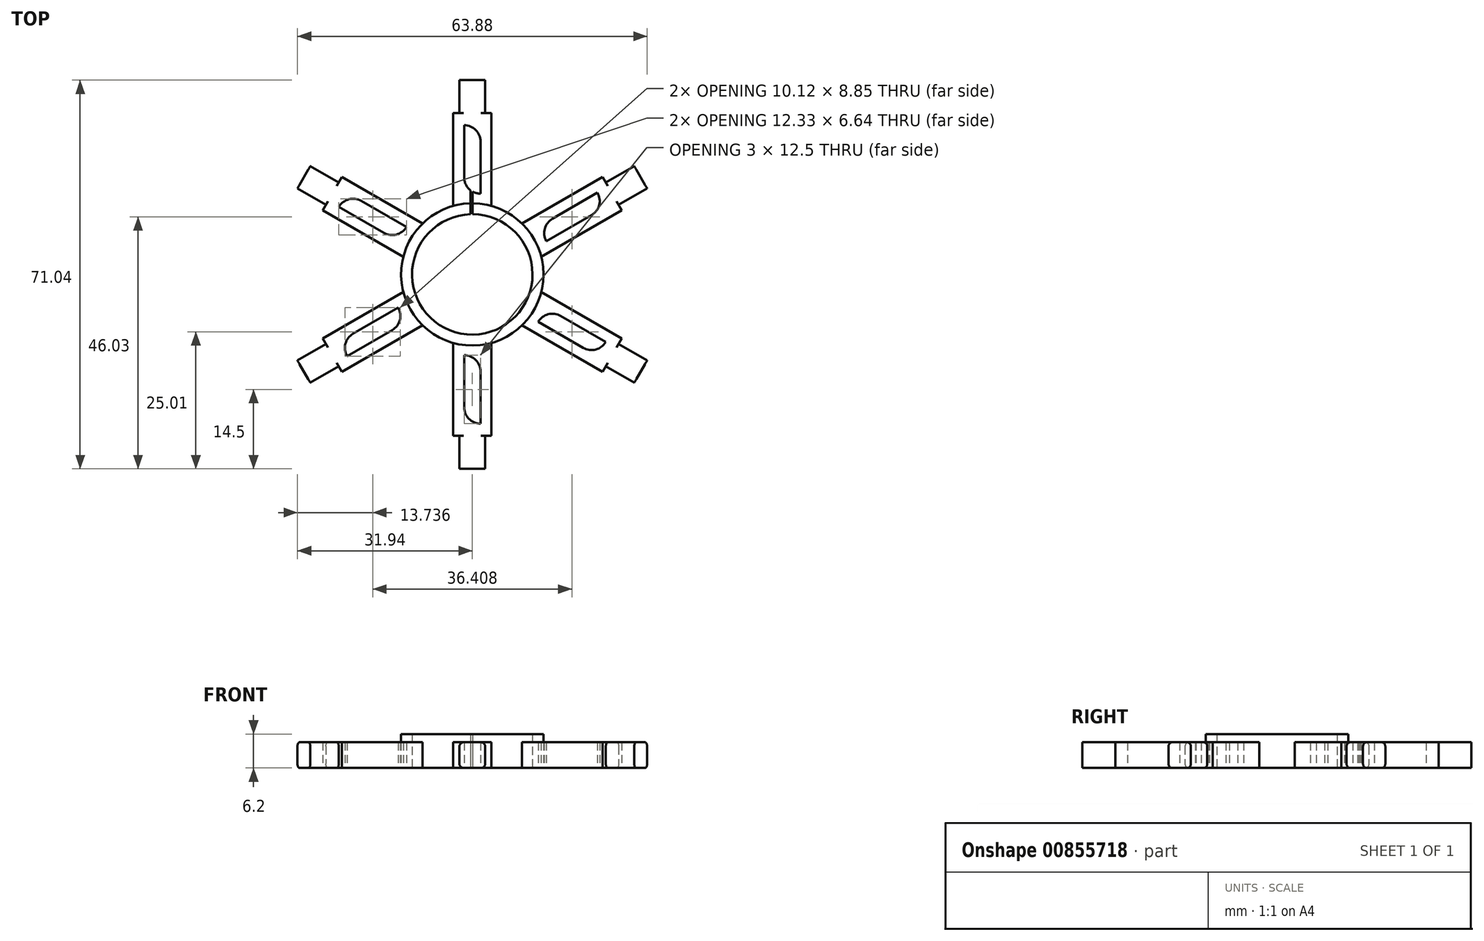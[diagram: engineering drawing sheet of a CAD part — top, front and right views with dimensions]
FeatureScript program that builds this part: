
annotation { "Feature Type Name" : "Feature", "Feature Type Description" : "" }
export const myFeature = defineFeature(function(context is Context, id is Id, definition is map)
    precondition{}
    {
        {
            var Q0;
            Q0=qCreatedBy(makeId("Top.planeOp"),FACE);
            var sketch = newSketch(context, id + "F0", { "sketchPlane" : qUnion([Q0])});
            skCircle(sketch, "E0", {"center": v(0, 0) * mm, "radius": 11 * mm});
            skCircle(sketch, "E1", {"center": v(0, 0) * mm, "radius": 13 * mm});
            skLineSegment(sketch, "E2.top", {"start": v(3.5, 29.52) * mm, "end": v(-3.5, 29.52) * mm});
            skLineSegment(sketch, "E2.left", {"start": v(3.5, 12.52) * mm, "end": v(3.5, 29.52) * mm});
            skLineSegment(sketch, "E2.right", {"start": v(-3.5, 12.52) * mm, "end": v(-3.5, 29.52) * mm});
            skPoint(sketch, "E2.middle", {"position": v(0, 21.02) * mm});
            skLineSegment(sketch, "E3.bottom", {"start": v(2.35, 29.52) * mm, "end": v(-2.35, 29.52) * mm});
            skLineSegment(sketch, "E3.top", {"start": v(2.35, 35.52) * mm, "end": v(-2.35, 35.52) * mm});
            skLineSegment(sketch, "E3.left", {"start": v(2.35, 29.52) * mm, "end": v(2.35, 35.52) * mm});
            skLineSegment(sketch, "E3.right", {"start": v(-2.35, 29.52) * mm, "end": v(-2.35, 35.52) * mm});
            skPoint(sketch, "E3.middle", {"position": v(0, 32.52) * mm});
            skLineSegment(sketch, "E4.bottom", {"start": v(1.5, 14.77) * mm, "end": v(1.5, 14.77) * mm});
            skLineSegment(sketch, "E4.top", {"start": v(-1.5, 27.27) * mm, "end": v(-1.5, 27.27) * mm});
            skLineSegment(sketch, "E4.left", {"start": v(1.5, 14.77) * mm, "end": v(1.5, 24.27) * mm});
            skLineSegment(sketch, "E4.right", {"start": v(-1.5, 17.77) * mm, "end": v(-1.5, 27.27) * mm});
            skPoint(sketch, "E5.visualSharp", {"position": v(-1.5, 14.77) * mm});
            skArc(sketch, "E5.filletArc", {"start": v(-1.5, 17.77) * mm, "mid": v(-0.62, 15.65) * mm, "end": v(1.5, 14.77) * mm});
            skPoint(sketch, "E6.visualSharp", {"position": v(1.5, 27.27) * mm});
            skArc(sketch, "E6.filletArc", {"start": v(1.5, 24.27) * mm, "mid": v(0.62, 26.4) * mm, "end": v(-1.5, 27.27) * mm});
            skSolve(sketch);
        }
        {
            var Q0;
            Q0=qCreatedBy(makeId("Top.planeOp"),FACE);
            var sketch = newSketch(context, id + "F1", { "sketchPlane" : qUnion([Q0])});
            skLineSegment(sketch, "E7.bottom", {"start": v(0.05, 15.5) * mm, "end": v(-0.3, 15.5) * mm});
            skLineSegment(sketch, "E7.top", {"start": v(0.05, 10.56) * mm, "end": v(-0.3, 10.56) * mm});
            skLineSegment(sketch, "E7.left", {"start": v(0.05, 15.5) * mm, "end": v(0.05, 10.56) * mm});
            skLineSegment(sketch, "E7.right", {"start": v(-0.3, 15.5) * mm, "end": v(-0.3, 10.56) * mm});
            skSolve(sketch);
        }
        {
            var Q0;
            Q0=makeQuery(id+"F0.imprint","IMPRINT",FACE,{"disambiguationData":[TD([[makeQuery(id+"F0.imprint","IMPRINT",EDGE,{"derivedFrom":sQuery(id+"F0.wireOp",EDGE,"E0")}),-1.0]])]});
            extrude(context, id + "F2", {"entities" : qUnion([Q0]), "depth" : 6.2 * mm, "offsetDistance" : 25.4 * mm});
        }
        {
            var Q0;
            {var subQ1=sQuery(id+"F0.wireOp",EDGE,"E2.left");Q0=makeQuery(id+"F0.imprint","IMPRINT",FACE,{"disambiguationData":[TD([[makeQuery(id+"F0.imprint","IMPRINT",EDGE,{"derivedFrom":subQ1}),1.0]])]});}
            var Q1;
            Q1=makeQuery(id+"F0.imprint","IMPRINT",FACE,{"disambiguationData":[TD([[makeQuery(id+"F0.imprint","IMPRINT",EDGE,{"derivedFrom":sQuery(id+"F0.wireOp",EDGE,"E3.top")}),1.0]])]});
            extrude(context, id + "F3", {"entities" : qUnion([Q0, Q1]), "operationType" : NewBodyOperationType.ADD, "depth" : 4.7 * mm, "offsetDistance" : 25.4 * mm});
        }
        {
            var Q0;
            Q0=makeQuery(id+"F2.opExtrude","SWEPT_BODY",BODY,{"disambiguationData":[OSD([sQuery(id+"F0.wireOp",EDGE,"E0"),sQuery(id+"F0.wireOp",EDGE,"E1")])]});
            var Q1;
            Q1=sQuery(id+"F0.wireOp",EDGE,"E0");
            circularPattern(context, id + "F4", {"operationType" : NewBodyOperationType.ADD, "entities" : qUnion([Q0]), "axis" : qUnion([Q1]), "angle" : 360 * degree, "instanceCount" : 6, "equalSpace" : true});
        }
        {
            var Q0;
            Q0 = qSketchRegion(id + "F1", true);
            extrude(context, id + "F5", {"entities" : qUnion([Q0]), "operationType" : NewBodyOperationType.REMOVE, "depth" : 25.4 * mm, "offsetDistance" : 25.4 * mm});
        }
        {
            var Q0;
            Q0=makeQuery(id+"F4.opPattern","COPY",EDGE,{"derivedFrom":makeQuery(id+"F3.opExtrude","CAP_EDGE",EDGE,{"disambiguationData":[OSD([sQuery(id+"F0.wireOp",EDGE,"E3.right")])],"isStart":false}),"instanceName":"2"});
            var Q1;
            Q1=makeQuery(id+"F4.opPattern","COPY",EDGE,{"derivedFrom":makeQuery(id+"F3.opExtrude","CAP_EDGE",EDGE,{"disambiguationData":[OSD([sQuery(id+"F0.wireOp",EDGE,"E3.left")])],"isStart":false}),"instanceName":"2"});
            var Q2;
            Q2=makeQuery(id+"F4.opPattern","COPY",EDGE,{"derivedFrom":makeQuery(id+"F3.opExtrude","CAP_EDGE",EDGE,{"disambiguationData":[OSD([sQuery(id+"F0.wireOp",EDGE,"E3.right")])],"isStart":true}),"instanceName":"2"});
            var Q3;
            Q3=makeQuery(id+"F4.opPattern","COPY",EDGE,{"derivedFrom":makeQuery(id+"F3.opExtrude","CAP_EDGE",EDGE,{"disambiguationData":[OSD([sQuery(id+"F0.wireOp",EDGE,"E3.left")])],"isStart":true}),"instanceName":"2"});
            var Q4;
            Q4=makeQuery(id+"F4.opPattern","COPY",EDGE,{"derivedFrom":makeQuery(id+"F3.opExtrude","CAP_EDGE",EDGE,{"disambiguationData":[OSD([sQuery(id+"F0.wireOp",EDGE,"E3.left")])],"isStart":true}),"instanceName":"3"});
            var Q5;
            Q5=makeQuery(id+"F4.opPattern","COPY",EDGE,{"derivedFrom":makeQuery(id+"F3.opExtrude","CAP_EDGE",EDGE,{"disambiguationData":[OSD([sQuery(id+"F0.wireOp",EDGE,"E3.left")])],"isStart":false}),"instanceName":"3"});
            var Q6;
            Q6=makeQuery(id+"F4.opPattern","COPY",EDGE,{"derivedFrom":makeQuery(id+"F3.opExtrude","CAP_EDGE",EDGE,{"disambiguationData":[OSD([sQuery(id+"F0.wireOp",EDGE,"E3.right")])],"isStart":false}),"instanceName":"3"});
            var Q7;
            Q7=makeQuery(id+"F4.opPattern","COPY",EDGE,{"derivedFrom":makeQuery(id+"F3.opExtrude","CAP_EDGE",EDGE,{"disambiguationData":[OSD([sQuery(id+"F0.wireOp",EDGE,"E3.right")])],"isStart":true}),"instanceName":"3"});
            var Q8;
            Q8=makeQuery(id+"F4.opPattern","COPY",EDGE,{"derivedFrom":makeQuery(id+"F3.opExtrude","CAP_EDGE",EDGE,{"disambiguationData":[OSD([sQuery(id+"F0.wireOp",EDGE,"E3.left")])],"isStart":false}),"instanceName":"4"});
            var Q9;
            Q9=makeQuery(id+"F4.opPattern","COPY",EDGE,{"derivedFrom":makeQuery(id+"F3.opExtrude","CAP_EDGE",EDGE,{"disambiguationData":[OSD([sQuery(id+"F0.wireOp",EDGE,"E3.left")])],"isStart":true}),"instanceName":"4"});
            var Q10;
            Q10=makeQuery(id+"F4.opPattern","COPY",EDGE,{"derivedFrom":makeQuery(id+"F3.opExtrude","CAP_EDGE",EDGE,{"disambiguationData":[OSD([sQuery(id+"F0.wireOp",EDGE,"E3.right")])],"isStart":false}),"instanceName":"4"});
            var Q11;
            Q11=makeQuery(id+"F4.opPattern","COPY",EDGE,{"derivedFrom":makeQuery(id+"F3.opExtrude","CAP_EDGE",EDGE,{"disambiguationData":[OSD([sQuery(id+"F0.wireOp",EDGE,"E3.right")])],"isStart":true}),"instanceName":"4"});
            var Q12;
            Q12=makeQuery(id+"F4.opPattern","COPY",EDGE,{"derivedFrom":makeQuery(id+"F3.opExtrude","CAP_EDGE",EDGE,{"disambiguationData":[OSD([sQuery(id+"F0.wireOp",EDGE,"E3.left")])],"isStart":false}),"instanceName":"5"});
            var Q13;
            Q13=makeQuery(id+"F4.opPattern","COPY",EDGE,{"derivedFrom":makeQuery(id+"F3.opExtrude","CAP_EDGE",EDGE,{"disambiguationData":[OSD([sQuery(id+"F0.wireOp",EDGE,"E3.left")])],"isStart":true}),"instanceName":"5"});
            var Q14;
            Q14=makeQuery(id+"F4.opPattern","COPY",EDGE,{"derivedFrom":makeQuery(id+"F3.opExtrude","CAP_EDGE",EDGE,{"disambiguationData":[OSD([sQuery(id+"F0.wireOp",EDGE,"E3.right")])],"isStart":false}),"instanceName":"5"});
            var Q15;
            Q15=makeQuery(id+"F4.opPattern","COPY",EDGE,{"derivedFrom":makeQuery(id+"F3.opExtrude","CAP_EDGE",EDGE,{"disambiguationData":[OSD([sQuery(id+"F0.wireOp",EDGE,"E3.right")])],"isStart":true}),"instanceName":"5"});
            var Q16;
            Q16=makeQuery(id+"F3.opExtrude","CAP_EDGE",EDGE,{"disambiguationData":[OSD([sQuery(id+"F0.wireOp",EDGE,"E3.left")])],"isStart":false});
            var Q17;
            Q17=makeQuery(id+"F3.opExtrude","CAP_EDGE",EDGE,{"disambiguationData":[OSD([sQuery(id+"F0.wireOp",EDGE,"E3.left")])],"isStart":true});
            var Q18;
            Q18=makeQuery(id+"F3.opExtrude","CAP_EDGE",EDGE,{"disambiguationData":[OSD([sQuery(id+"F0.wireOp",EDGE,"E3.right")])],"isStart":false});
            var Q19;
            Q19=makeQuery(id+"F3.opExtrude","CAP_EDGE",EDGE,{"disambiguationData":[OSD([sQuery(id+"F0.wireOp",EDGE,"E3.right")])],"isStart":true});
            var Q20;
            Q20=makeQuery(id+"F4.opPattern","COPY",EDGE,{"derivedFrom":makeQuery(id+"F3.opExtrude","CAP_EDGE",EDGE,{"disambiguationData":[OSD([sQuery(id+"F0.wireOp",EDGE,"E3.left")])],"isStart":false}),"instanceName":"1"});
            var Q21;
            Q21=makeQuery(id+"F4.opPattern","COPY",EDGE,{"derivedFrom":makeQuery(id+"F3.opExtrude","CAP_EDGE",EDGE,{"disambiguationData":[OSD([sQuery(id+"F0.wireOp",EDGE,"E3.left")])],"isStart":true}),"instanceName":"1"});
            var Q22;
            Q22=makeQuery(id+"F4.opPattern","COPY",EDGE,{"derivedFrom":makeQuery(id+"F3.opExtrude","CAP_EDGE",EDGE,{"disambiguationData":[OSD([sQuery(id+"F0.wireOp",EDGE,"E3.right")])],"isStart":false}),"instanceName":"1"});
            var Q23;
            Q23=makeQuery(id+"F4.opPattern","COPY",EDGE,{"derivedFrom":makeQuery(id+"F3.opExtrude","CAP_EDGE",EDGE,{"disambiguationData":[OSD([sQuery(id+"F0.wireOp",EDGE,"E3.right")])],"isStart":true}),"instanceName":"1"});
            fillet(context, id + "F6", {"entities" : qUnion([Q0, Q1, Q2, Q3, Q4, Q5, Q6, Q7, Q8, Q9, Q10, Q11, Q12, Q13, Q14, Q15, Q16, Q17, Q18, Q19, Q20, Q21, Q22, Q23]), "radius" : 0.76 * mm, "tangentPropagation" : true, "allowEdgeOverflow" : false});
        }
    });
